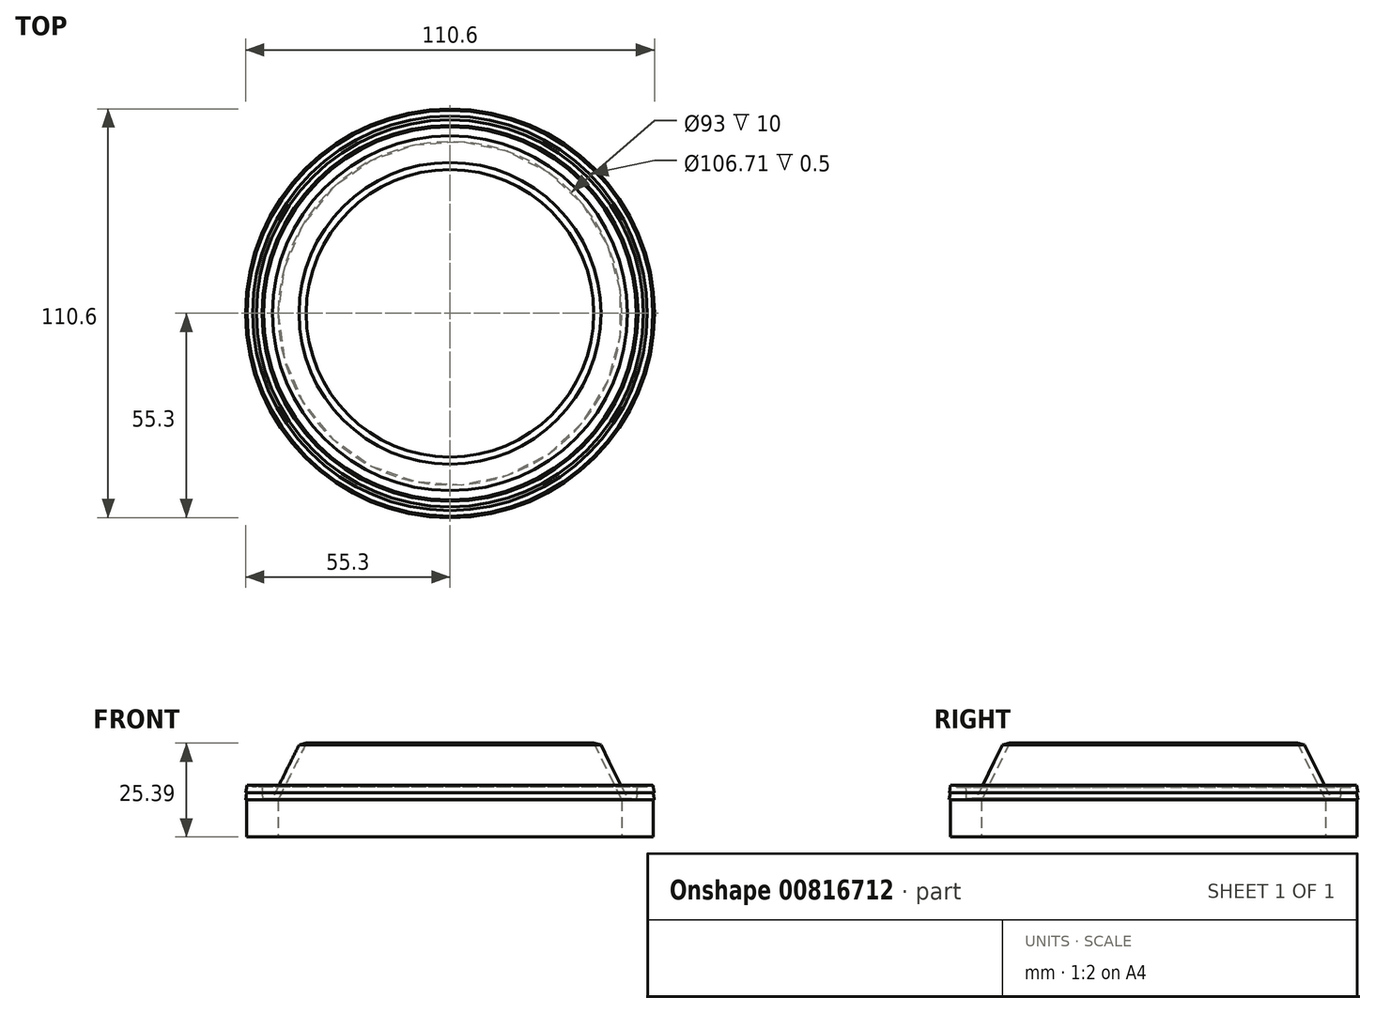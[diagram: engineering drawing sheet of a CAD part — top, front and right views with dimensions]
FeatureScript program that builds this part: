
annotation { "Feature Type Name" : "Feature", "Feature Type Description" : "" }
export const myFeature = defineFeature(function(context is Context, id is Id, definition is map)
    precondition{}
    {
        {
            var Q0;
            Q0=qCreatedBy(makeId("Top.planeOp"),FACE);
            var sketch = newSketch(context, id + "F0", { "sketchPlane" : qUnion([Q0])});
            skCircle(sketch, "E0", {"center": v(0, 0) * mm, "radius": 46.5 * mm});
            skCircle(sketch, "E1.0", {"center": v(0, 0) * mm, "radius": 55 * mm});
            skSolve(sketch);
        }
        {
            var Q0;
            Q0=makeQuery(id+"F0.imprint","IMPRINT",FACE,{"disambiguationData":[TD([[makeQuery(id+"F0.imprint","IMPRINT",EDGE,{"derivedFrom":sQuery(id+"F0.wireOp",EDGE,"E0")}),-1.0]])]});
            extrude(context, id + "F1", {"entities" : qUnion([Q0]), "depth" : 10 * mm, "offsetDistance" : 25 * mm});
        }
        {
            var Q0;
            Q0=makeQuery(id+"F1.opExtrude","CAP_FACE",FACE,{"disambiguationData":[OSD([sQuery(id+"F0.wireOp",EDGE,"E0"),sQuery(id+"F0.wireOp",EDGE,"E1.0")])],"isStart":false});
            var sketch = newSketch(context, id + "F2", { "sketchPlane" : qUnion([Q0])});
            skCircle(sketch, "E2.0", {"center": v(0, 0) * mm, "radius": 50.75 * mm});
            skCircle(sketch, "E3.0", {"center": v(0, 0) * mm, "radius": 50.45 * mm});
            skCircle(sketch, "E4.0", {"center": v(0, 0) * mm, "radius": 55.3 * mm});
            skSolve(sketch);
        }
        {
            var Q0;
            Q0=makeQuery(id+"F2.imprint","IMPRINT",FACE,{"disambiguationData":[TD([[makeQuery(id+"F2.imprint","IMPRINT",EDGE,{"derivedFrom":sQuery(id+"F2.wireOp",EDGE,"E2.0")}),-1.0]])]});
            var Q1;
            Q1=makeQuery(id+"F2.imprint","IMPRINT",FACE,{"disambiguationData":[TD([[makeQuery(id+"F2.imprint","IMPRINT",EDGE,{"derivedFrom":sQuery(id+"F2.wireOp",EDGE,"E2.0")}),1.0]])]});
            var Q2;
            Q2=makeQuery(id+"F2.imprint","IMPRINT",FACE,{"disambiguationData":[TD([[makeQuery(id+"F2.imprint","IMPRINT",EDGE,{"derivedFrom":sQuery(id+"F2.wireOp",EDGE,"E4.0")}),1.0]])]});
            extrude(context, id + "F3", {"entities" : qUnion([Q0, Q1, Q2]), "operationType" : NewBodyOperationType.ADD, "depth" : 2 * mm, "offsetDistance" : 25 * mm, "hasDraft" : true, "draftAngle" : 10 * degree, "draftPullDirection" : true});
        }
        {
            var Q0;
            Q0=makeQuery(id+"F3.opExtrude","CAP_FACE",FACE,{"disambiguationData":[OSD([sQuery(id+"F2.wireOp",EDGE,"E3.0"),sQuery(id+"F2.wireOp",EDGE,"E4.0")])],"isStart":false});
            var sketch = newSketch(context, id + "F4", { "sketchPlane" : qUnion([Q0])});
            skCircle(sketch, "E5.0", {"center": v(0, 0) * mm, "radius": 50.5 * mm});
            skCircle(sketch, "E6.0", {"center": v(0, 0) * mm, "radius": 55.25 * mm});
            skSolve(sketch);
        }
        {
            var Q0;
            Q0=makeQuery(id+"F4.imprint","IMPRINT",FACE,{"disambiguationData":[TD([[makeQuery(id+"F4.imprint","IMPRINT",EDGE,{"derivedFrom":sQuery(id+"F4.wireOp",EDGE,"E6.0")}),1.0]])]});
            var Q1;
            Q1=makeQuery(id+"F4.imprint","IMPRINT",FACE,{"disambiguationData":[TD([[makeQuery(id+"F4.imprint","IMPRINT",EDGE,{"derivedFrom":makeQuery(id+"F3.opExtrude","CAP_EDGE",EDGE,{"disambiguationData":[OSD([sQuery(id+"F2.wireOp",EDGE,"E3.0")])],"isStart":false})}),-1.0]])]});
            var Q2;
            Q2=makeQuery(id+"F4.imprint","IMPRINT",FACE,{"disambiguationData":[TD([[makeQuery(id+"F4.imprint","IMPRINT",EDGE,{"derivedFrom":sQuery(id+"F4.wireOp",EDGE,"E5.0")}),-1.0]])]});
            extrude(context, id + "F5", {"entities" : qUnion([Q0, Q1, Q2]), "operationType" : NewBodyOperationType.ADD, "depth" : 2 * mm, "offsetDistance" : 25 * mm, "hasDraft" : true, "draftAngle" : 10 * degree, "draftPullDirection" : true});
        }
        {
            var Q0;
            Q0=makeQuery(id+"F5.opExtrude","CAP_FACE",FACE,{"disambiguationData":[OSD([sQuery(id+"F4.wireOp",EDGE,"E5.0"),sQuery(id+"F4.wireOp",EDGE,"E6.0")])],"isStart":false});
            var sketch = newSketch(context, id + "F6", { "sketchPlane" : qUnion([Q0])});
            skCircle(sketch, "E7.0", {"center": v(0, 0) * mm, "radius": 53.36 * mm});
            skCircle(sketch, "E8.0", {"center": v(0, 0) * mm, "radius": 52.36 * mm});
            skSolve(sketch);
        }
        {
            var Q0;
            Q0=makeQuery(id+"F6.imprint","IMPRINT",FACE,{"disambiguationData":[TD([[makeQuery(id+"F6.imprint","IMPRINT",EDGE,{"derivedFrom":sQuery(id+"F6.wireOp",EDGE,"E7.0")}),1.0]])]});
            extrude(context, id + "F7", {"entities" : qUnion([Q0]), "operationType" : NewBodyOperationType.REMOVE, "oppositeDirection" : true, "depth" : 0.5 * mm, "offsetDistance" : 25 * mm});
        }
        {
            var Q0;
            Q0=qCreatedBy(makeId("Front.planeOp"),FACE);
            var sketch = newSketch(context, id + "F8", { "sketchPlane" : qUnion([Q0])});
            skLineSegment(sketch, "E9", {"start": v(-50.44, 10) * mm, "end": v(-46.5, 10) * mm});
            skLineSegment(sketch, "E10", {"start": v(-46.5, 10) * mm, "end": v(-38.9, 25.39) * mm});
            skLineSegment(sketch, "E11", {"start": v(-38.9, 25.39) * mm, "end": v(-40.82, 24.86) * mm});
            skLineSegment(sketch, "E12", {"start": v(-41.71, 19.69) * mm, "end": v(-43.08, 20.36) * mm});
            skLineSegment(sketch, "E13", {"start": v(-43.08, 20.36) * mm, "end": v(-40.82, 24.86) * mm});
            skLineSegment(sketch, "E14", {"start": v(-43.08, 20.36) * mm, "end": v(-48.2, 10) * mm});
            skLineSegment(sketch, "E15", {"start": v(-50.44, 10) * mm, "end": v(-50.44, 10.4) * mm});
            skLineSegment(sketch, "E16", {"start": v(-50.44, 10.4) * mm, "end": v(-48.2, 10.4) * mm});
            skLineSegment(sketch, "E17", {"start": v(-48.2, 10.4) * mm, "end": v(-48, 10.4) * mm});
            skSolve(sketch);
        }
        {
            var Q0;
            {var subQ0=sQuery(id+"F8.wireOp",EDGE,"E11");Q0=makeQuery(id+"F8.imprint","IMPRINT",FACE,{"disambiguationData":[TD([[makeQuery(id+"F8.imprint","IMPRINT",EDGE,{"derivedFrom":subQ0}),1.0]])]});}
            var Q1;
            {var subQ0=sQuery(id+"F8.wireOp",EDGE,"E12");Q1=makeQuery(id+"F8.imprint","IMPRINT",FACE,{"disambiguationData":[TD([[makeQuery(id+"F8.imprint","IMPRINT",EDGE,{"derivedFrom":subQ0}),1.0]])]});}
            var Q2;
            {var subQ0=sQuery(id+"F8.wireOp",EDGE,"E15");Q2=makeQuery(id+"F8.imprint","IMPRINT",FACE,{"disambiguationData":[TD([[makeQuery(id+"F8.imprint","IMPRINT",EDGE,{"derivedFrom":subQ0}),-1.0]])]});}
            var Q3;
            Q3=makeQuery(id+"F1.opExtrude","SWEPT_FACE",FACE,{"disambiguationData":[OSD([sQuery(id+"F0.wireOp",EDGE,"E0")])]});
            revolve(context, id + "F9", {"operationType" : NewBodyOperationType.ADD, "surfaceOperationType" : NewSurfaceOperationType.NEW, "entities" : qUnion([Q0, Q1, Q2]), "axis" : qUnion([Q3]), "revolveType" : RevolveType.FULL});
        }
    });
